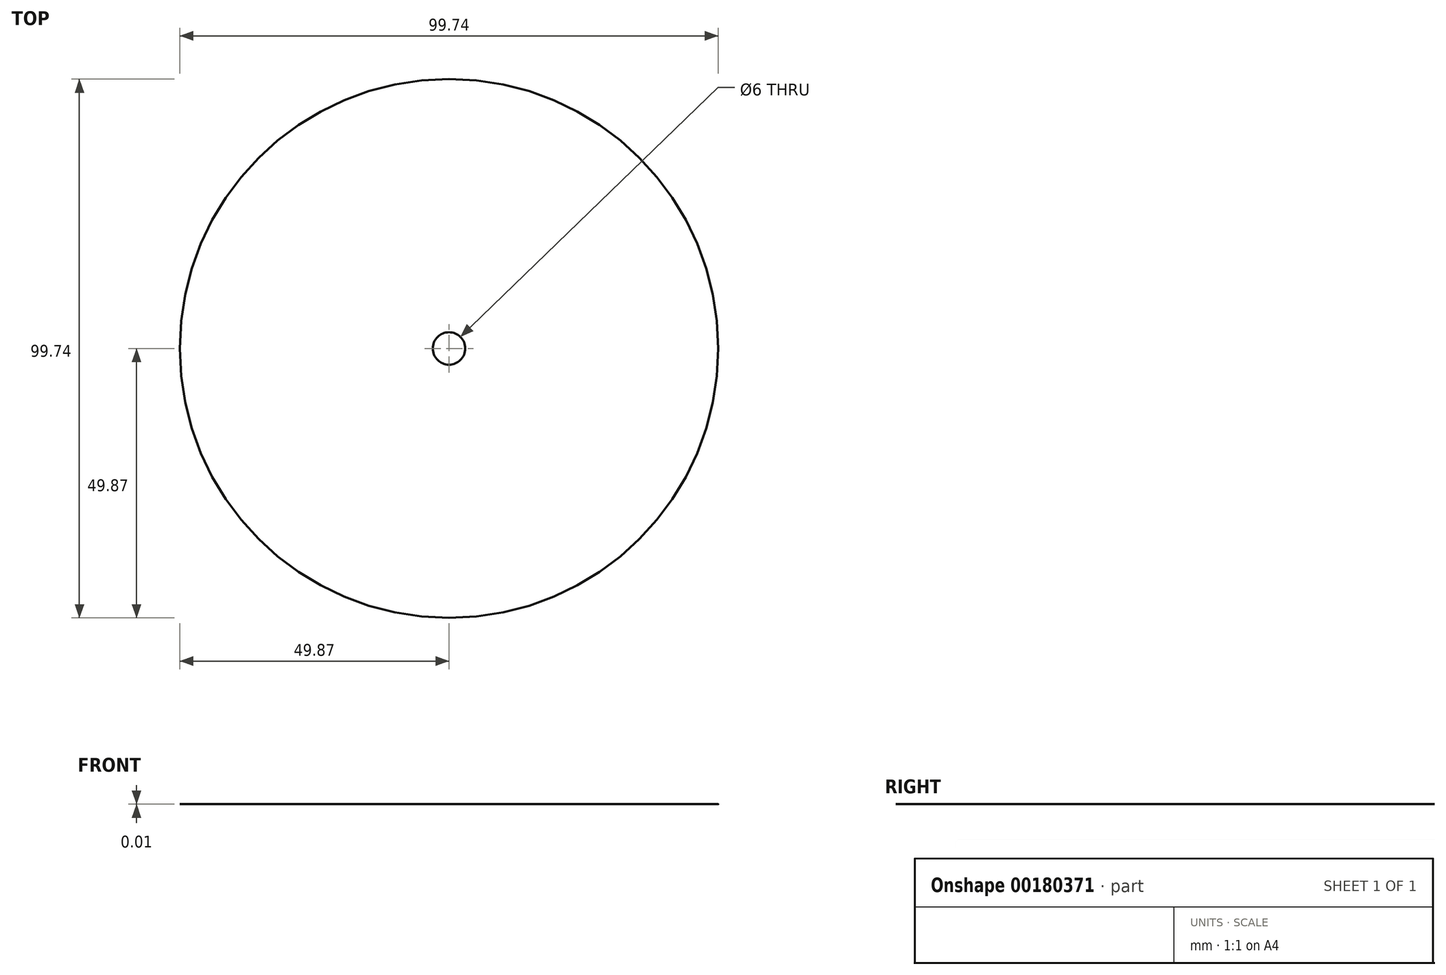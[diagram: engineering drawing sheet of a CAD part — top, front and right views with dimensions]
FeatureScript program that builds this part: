
annotation { "Feature Type Name" : "Feature", "Feature Type Description" : "" }
export const myFeature = defineFeature(function(context is Context, id is Id, definition is map)
    precondition{}
    {
        {
            var Q0;
            Q0=qCreatedBy(makeId("Top.planeOp"),FACE);
            var sketch = newSketch(context, id + "F0", { "sketchPlane" : qUnion([Q0])});
            skCircle(sketch, "E0", {"center": v(0, 0) * mm, "radius": 49.87 * mm});
            skCircle(sketch, "E1", {"center": v(0, 0) * mm, "radius": 3 * mm});
            skSolve(sketch);
        }
        {
            var Q0;
            Q0 = qSketchRegion(id + "F0", true);
            extrude(context, id + "F1", {"entities" : qUnion([Q0]), "depth" : 3 / 406.4 * mm});
        }
    });
